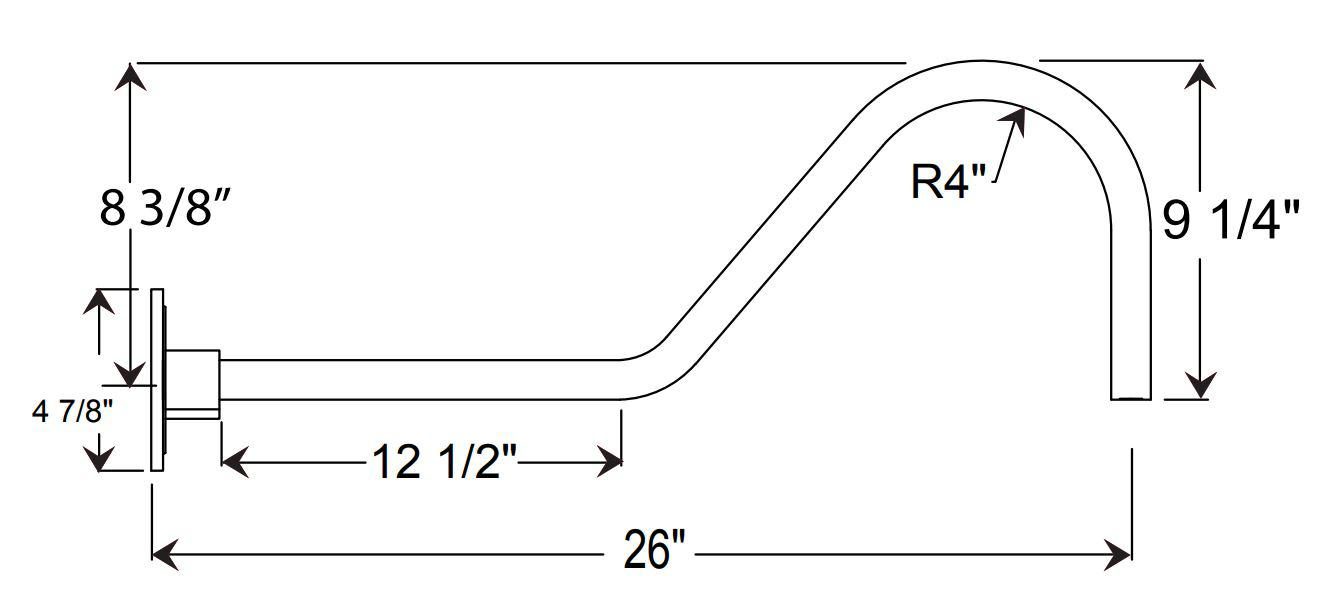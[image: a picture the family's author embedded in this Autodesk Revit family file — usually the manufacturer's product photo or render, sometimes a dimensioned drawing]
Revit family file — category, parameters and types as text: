
# Revit family: OSPBF LED 12,20,24
name_source: partatom
category: Lighting Fixtures
units: mm (PartAtom-declared; Revit-internal decimal feet)

## family parameters
Always vertical = Yes
Cut with Voids When Loaded = No
Light Source = Yes
OmniClass Number = 23.80.70.00
OmniClass Title = Lighting
Part Type = Normal
Room Calculation Point = No
Round Connector Dimension = Use Diameter
Shared = No
Work Plane-Based = No

## types (3) — shared parameters
Apparent Load = 24 VA
Body Colour = Spun aluminium
Body Material = body
CRI = >90
Canopy Body = GY
Color Filter = 16777215
Construction Material = Heavy Duty spun aluminum.
Default Elevation = 0' - 0"
Description = 120-277 Voltage
Dimming = 1%
Dimming Lamp Color Temperature Shift = <None>
Efficiency = 97-125 lumens per watt
HUB = body
Lamp = LED
Life = L70 50,000 hours
Load Classification = Lighting
Manufacturer = ANP Lighting
Photometric Web File = generic
Power Factor = 1
Tilt Angle = 90.00°
URL = https://www.anplighting.com
Voltage = 277 V
Warranty = 5 year limited warranty
Wattage Comments = 24 W
b = 0' - 3"

## per-type parameters (varying)
| type | Bulb | Fixture Diameter | Fixture Height | OSPBF12 | OSPBF20 | OSPBF24 | Weight | a |
| OSPBF12 | Bulb | 1' - 0" | 1' - 9" | Yes | No | No | 7.0 lbs | 1' - 3" |
| OSPBF20 | Glass | 1' - 8" | 2' - 11" | No | Yes | No | 11.0 lbs | 1' - 7" |
| OSPBF24 | Glass | 2' - 0" | 3' - 6" | No | No | Yes | 14.0 lbs | 1' - 10" |

note: column(s) folded — value = type name in every type: Model

## geometry (parser evidence)
native form markers: Sweep x35
no freeform markers — native parametric forms only
